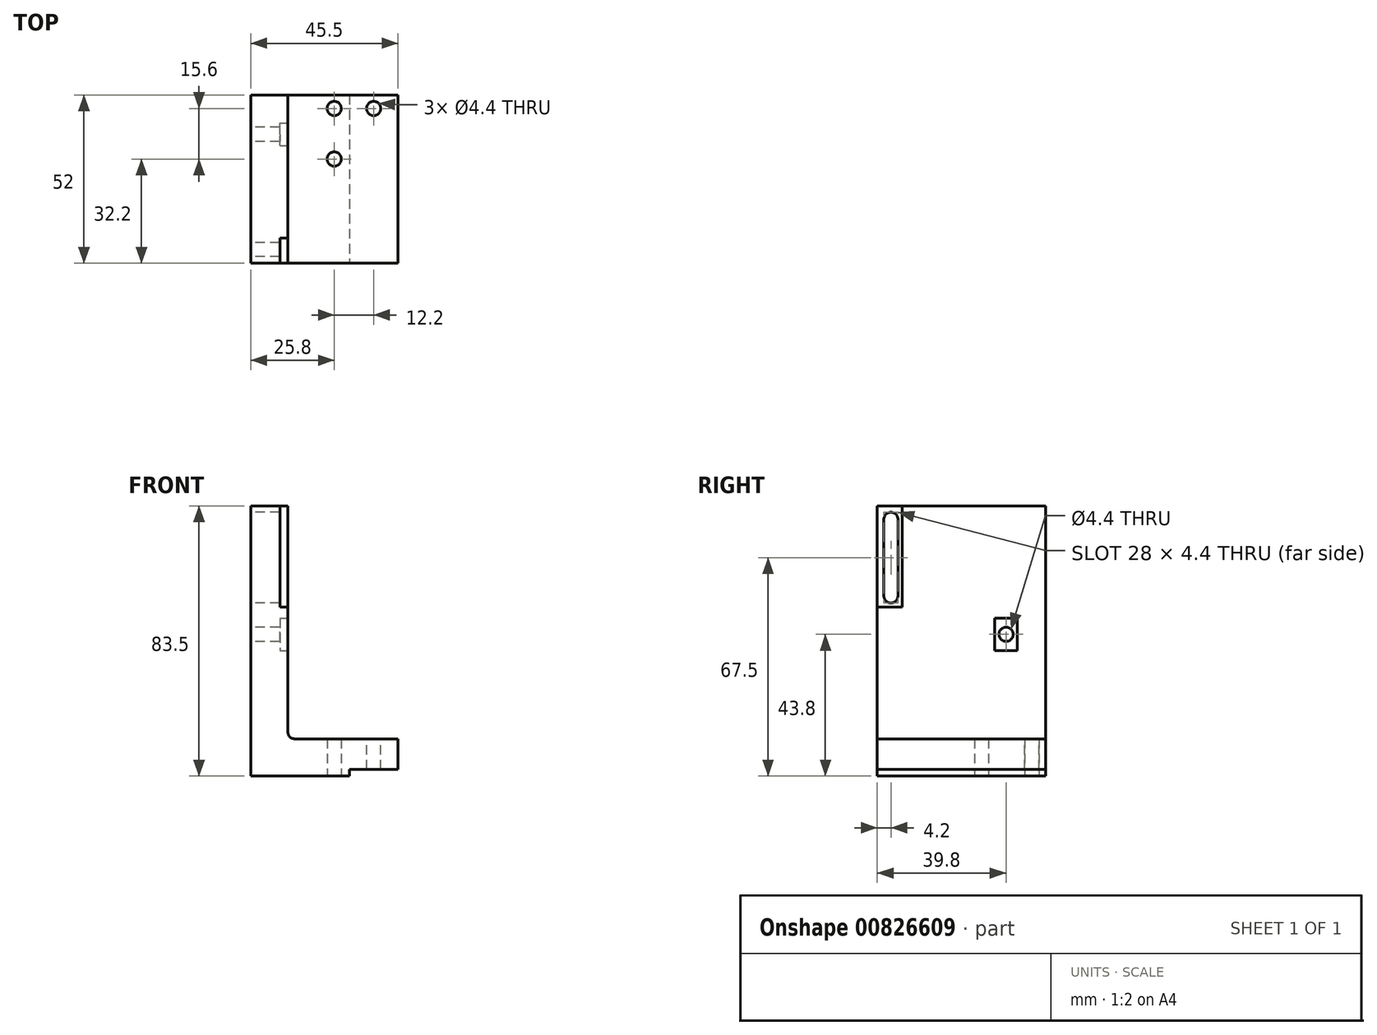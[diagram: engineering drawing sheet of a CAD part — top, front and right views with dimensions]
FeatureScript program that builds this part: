
annotation { "Feature Type Name" : "Feature", "Feature Type Description" : "" }
export const myFeature = defineFeature(function(context is Context, id is Id, definition is map)
    precondition{}
    {
        {
            var Q0;
            Q0=qCreatedBy(makeId("Front.planeOp"),FACE);
            var sketch = newSketch(context, id + "F0", { "sketchPlane" : qUnion([Q0])});
            skLineSegment(sketch, "E0.bottom", {"start": v(-11.5, 72) * mm, "end": v(34, 72) * mm});
            skLineSegment(sketch, "E0.top", {"start": v(-11.5, -11.5) * mm, "end": v(34, -11.5) * mm});
            skLineSegment(sketch, "E0.left", {"start": v(-11.5, 72) * mm, "end": v(-11.5, -11.5) * mm});
            skLineSegment(sketch, "E0.right", {"start": v(34, 72) * mm, "end": v(34, -11.5) * mm});
            skSolve(sketch);
        }
        {
            var Q0;
            Q0=qSketchRegion(id+"F0",true);
            extrude(context, id + "F1", {"entities" : qUnion([Q0]), "depth" : 52 * mm, "offsetDistance" : 25 * mm});
        }
        {
            var Q0;
            Q0=makeQuery(id+"F1.opExtrude","CAP_FACE",FACE,{"disambiguationData":[OSD([sQuery(id+"F0.wireOp",EDGE,"E0.bottom"),sQuery(id+"F0.wireOp",EDGE,"E0.top"),sQuery(id+"F0.wireOp",EDGE,"E0.left"),sQuery(id+"F0.wireOp",EDGE,"E0.right")])],"isStart":false});
            var sketch = newSketch(context, id + "F2", { "sketchPlane" : qUnion([Q0])});
            skLineSegment(sketch, "E1.bottom", {"start": v(34, 72) * mm, "end": v(0, 72) * mm});
            skLineSegment(sketch, "E1.top", {"start": v(34, 0) * mm, "end": v(0, 0) * mm});
            skLineSegment(sketch, "E1.left", {"start": v(34, 72) * mm, "end": v(34, 0) * mm});
            skLineSegment(sketch, "E1.right", {"start": v(0, 72) * mm, "end": v(0, 0) * mm});
            skSolve(sketch);
        }
        {
            var Q0;
            Q0=qSketchRegion(id+"F2",true);
            extrude(context, id + "F3", {"entities" : qUnion([Q0]), "operationType" : NewBodyOperationType.REMOVE, "endBound" : BoundingType.THROUGH_ALL, "oppositeDirection" : true, "depth" : 52 * mm, "offsetDistance" : 25 * mm});
        }
        {
            var Q0;
            Q0=makeQuery(id+"F1.opExtrude","SWEPT_FACE",FACE,{"disambiguationData":[OSD([sQuery(id+"F0.wireOp",EDGE,"E0.top")])]});
            var sketch = newSketch(context, id + "F4", { "sketchPlane" : qUnion([Q0])});
            skPoint(sketch, "E2", {"position": v(14.3, 4.2) * mm});
            skPoint(sketch, "E3", {"position": v(14.3, 19.8) * mm});
            skSolve(sketch);
        }
        {
            var Q0;
            Q0=makeQuery(id+"F1.opExtrude","CAP_FACE",FACE,{"disambiguationData":[OSD([sQuery(id+"F0.wireOp",EDGE,"E0.bottom"),sQuery(id+"F0.wireOp",EDGE,"E0.top"),sQuery(id+"F0.wireOp",EDGE,"E0.left"),sQuery(id+"F0.wireOp",EDGE,"E0.right")])],"isStart":false});
            var sketch = newSketch(context, id + "F5", { "sketchPlane" : qUnion([Q0])});
            skLineSegment(sketch, "E4.bottom", {"start": v(34, -11.5) * mm, "end": v(19, -11.5) * mm});
            skLineSegment(sketch, "E4.top", {"start": v(34, -9.5) * mm, "end": v(19, -9.5) * mm});
            skLineSegment(sketch, "E4.left", {"start": v(34, -11.5) * mm, "end": v(34, -9.5) * mm});
            skLineSegment(sketch, "E4.right", {"start": v(19, -11.5) * mm, "end": v(19, -9.5) * mm});
            skSolve(sketch);
        }
        {
            var Q0;
            Q0=qSketchRegion(id+"F5",true);
            extrude(context, id + "F6", {"entities" : qUnion([Q0]), "operationType" : NewBodyOperationType.REMOVE, "endBound" : BoundingType.THROUGH_ALL, "oppositeDirection" : true, "depth" : 25 * mm, "offsetDistance" : 25 * mm});
        }
        {
            var Q0;
            Q0=makeQuery(id+"F3.boolean.opBoolean","COPY",FACE,{"derivedFrom":makeQuery(id+"F3.opExtrude","SWEPT_FACE",FACE,{"disambiguationData":[OSD([sQuery(id+"F2.wireOp",EDGE,"E1.top")])]})});
            var sketch = newSketch(context, id + "F7", { "sketchPlane" : qUnion([Q0])});
            skPoint(sketch, "E5", {"position": v(26.5, -4.2) * mm});
            skSolve(sketch);
        }
        {
            var Q0;
            Q0=makeQuery(id+"F3.boolean.opBoolean","COPY",EDGE,{"derivedFrom":makeQuery(id+"F3.opExtrude","SWEPT_EDGE",EDGE,{"disambiguationData":[OSD([sQuery(id+"F2.wireOp",EDGE,"E1.top"),sQuery(id+"F2.wireOp",EDGE,"E1.right")])]})});
            fillet(context, id + "F8", {"entities" : qUnion([Q0]), "radius" : 2 * mm, "tangentPropagation" : true, "allowEdgeOverflow" : false});
        }
        {
            var Q0;
            Q0=makeQuery(id+"F1.opExtrude","SWEPT_FACE",FACE,{"disambiguationData":[OSD([sQuery(id+"F0.wireOp",EDGE,"E0.left")])]});
            var sketch = newSketch(context, id + "F9", { "sketchPlane" : qUnion([Q0])});
            skPoint(sketch, "E6", {"position": v(12.2, 32.3) * mm});
            skSolve(sketch);
        }
        {
            var Q0;
            Q0=sQuery(id+"F7.wireOp",VERTEX,"E5");
            var Q1;
            Q1=sQuery(id+"F9.wireOp",VERTEX,"E6");
            var Q2;
            Q2=sQuery(id+"F4.wireOp",VERTEX,"9ac88c87-b674-4f94-b65b-44ee802f1d45");
            var Q3;
            Q3=sQuery(id+"F4.wireOp",VERTEX,"E3");
            var Q4;
            Q4=sQuery(id+"F4.wireOp",VERTEX,"E2");
            var Q5;
            Q5=makeQuery(id+"F1.opExtrude","SWEPT_BODY",BODY,{"disambiguationData":[OSD([sQuery(id+"F0.wireOp",EDGE,"E0.bottom"),sQuery(id+"F0.wireOp",EDGE,"E0.top"),sQuery(id+"F0.wireOp",EDGE,"E0.left"),sQuery(id+"F0.wireOp",EDGE,"E0.right")])]});
            hole(context, id + "F10", {"style" : HoleStyle.SIMPLE, "endStyle" : HoleEndStyle.THROUGH, "standardTappedOrClearance" : lookupTablePath({ "standard" : "ISO", "fit" : "Normal", "size" : "M4", "type" : "Clearance" }), "standardBlindInLast" : lookupTablePath({ "fit" : "Standard", "standard" : "ISO", "size" : "M4", "type" : "Clearance" }), "holeDiameter" : 4.4 * mm, "majorDiameter" : 5 * mm, "isTappedThrough" : true, "tappedDepth" : 12 * mm, "tapClearance" : 3, "locations" : qUnion([Q0, Q1, Q2, Q3, Q4]), "scope" : qUnion([Q5])});
        }
        {
            var Q0;
            Q0=makeQuery(id+"F1.opExtrude","SWEPT_FACE",FACE,{"disambiguationData":[OSD([sQuery(id+"F0.wireOp",EDGE,"E0.left")])]});
            var sketch = newSketch(context, id + "F11", { "sketchPlane" : qUnion([Q0])});
            skLineSegment(sketch, "E7.bottom", {"start": v(47.8, 70) * mm, "end": v(47.8, 70) * mm});
            skLineSegment(sketch, "E7.top", {"start": v(47.8, 42) * mm, "end": v(47.8, 42) * mm});
            skLineSegment(sketch, "E7.left", {"start": v(45.6, 67.8) * mm, "end": v(45.6, 44.2) * mm});
            skLineSegment(sketch, "E7.right", {"start": v(50, 67.8) * mm, "end": v(50, 44.2) * mm});
            skPoint(sketch, "E8.visualSharp", {"position": v(50, 70) * mm});
            skArc(sketch, "E8.filletArc", {"start": v(50, 67.8) * mm, "mid": v(49.36, 69.36) * mm, "end": v(47.8, 70) * mm});
            skPoint(sketch, "E9.visualSharp", {"position": v(45.6, 70) * mm});
            skArc(sketch, "E9.filletArc", {"start": v(47.8, 70) * mm, "mid": v(46.24, 69.36) * mm, "end": v(45.6, 67.8) * mm});
            skPoint(sketch, "E10.visualSharp", {"position": v(50, 42) * mm});
            skArc(sketch, "E10.filletArc", {"start": v(47.8, 42) * mm, "mid": v(49.36, 42.64) * mm, "end": v(50, 44.2) * mm});
            skPoint(sketch, "E11.visualSharp", {"position": v(45.6, 42) * mm});
            skArc(sketch, "E11.filletArc", {"start": v(45.6, 44.2) * mm, "mid": v(46.24, 42.64) * mm, "end": v(47.8, 42) * mm});
            skSolve(sketch);
        }
        {
            var Q0;
            Q0=qSketchRegion(id+"F11",true);
            extrude(context, id + "F12", {"entities" : qUnion([Q0]), "operationType" : NewBodyOperationType.REMOVE, "endBound" : BoundingType.THROUGH_ALL, "oppositeDirection" : true, "depth" : 25 * mm, "offsetDistance" : 25 * mm});
        }
        {
            var Q0;
            Q0=makeQuery(id+"F3.boolean.opBoolean","COPY",FACE,{"derivedFrom":makeQuery(id+"F3.opExtrude","SWEPT_FACE",FACE,{"disambiguationData":[OSD([sQuery(id+"F2.wireOp",EDGE,"E1.right")])]})});
            var sketch = newSketch(context, id + "F13", { "sketchPlane" : qUnion([Q0])});
            skLineSegment(sketch, "E12.bottom", {"start": v(-15.7, 37.3) * mm, "end": v(-8.7, 37.3) * mm});
            skLineSegment(sketch, "E12.top", {"start": v(-15.7, 27.3) * mm, "end": v(-8.7, 27.3) * mm});
            skLineSegment(sketch, "E12.left", {"start": v(-15.7, 37.3) * mm, "end": v(-15.7, 27.3) * mm});
            skLineSegment(sketch, "E12.right", {"start": v(-8.7, 37.3) * mm, "end": v(-8.7, 27.3) * mm});
            skSolve(sketch);
        }
        {
            var Q0;
            Q0=qSketchRegion(id+"F13",true);
            extrude(context, id + "F14", {"entities" : qUnion([Q0]), "operationType" : NewBodyOperationType.REMOVE, "oppositeDirection" : true, "depth" : 2.5 * mm, "offsetDistance" : 25 * mm});
        }
        {
            var Q0;
            Q0=makeQuery(id+"F3.boolean.opBoolean","COPY",FACE,{"derivedFrom":makeQuery(id+"F3.opExtrude","SWEPT_FACE",FACE,{"disambiguationData":[OSD([sQuery(id+"F2.wireOp",EDGE,"E1.right")])]})});
            var sketch = newSketch(context, id + "F15", { "sketchPlane" : qUnion([Q0])});
            skLineSegment(sketch, "E13.bottom", {"start": v(-52, 40.7) * mm, "end": v(-44.3, 40.7) * mm});
            skLineSegment(sketch, "E13.top", {"start": v(-52, 72) * mm, "end": v(-44.3, 72) * mm});
            skLineSegment(sketch, "E13.left", {"start": v(-44.3, 40.7) * mm, "end": v(-44.3, 72) * mm});
            skLineSegment(sketch, "E13.right", {"start": v(-52, 40.7) * mm, "end": v(-52, 72) * mm});
            skSolve(sketch);
        }
        {
            var Q0;
            Q0=makeQuery(id+"F15.imprint","IMPRINT",FACE,{"disambiguationData":[TD([[makeQuery(id+"F15.imprint","IMPRINT",EDGE,{"derivedFrom":sQuery(id+"F15.wireOp",EDGE,"E13.bottom")}),1.0]])]});
            extrude(context, id + "F16", {"entities" : qUnion([Q0]), "operationType" : NewBodyOperationType.REMOVE, "oppositeDirection" : true, "depth" : 2.5 * mm, "offsetDistance" : 25 * mm});
        }
    });
